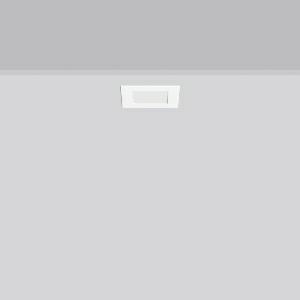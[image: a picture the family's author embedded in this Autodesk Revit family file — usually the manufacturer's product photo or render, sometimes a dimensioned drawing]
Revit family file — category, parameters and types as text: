
# Revit family: toledo_flat_square_e_672241_002_89_4ca7
name_source: partatom
category: Lighting Fixtures
units: mm (PartAtom-declared; Revit-internal decimal feet)

## family parameters
Cut with Voids When Loaded = No
Host = Face
Light Source = No
Part Type = Normal
Room Calculation Point = No
Round Connector Dimension = Use Diameter
Shared = No

## types (1)
- TOLEDO FLAT square E (1 x LED Modul 830, 370 lm, 3000)
    Apparent Load = 6 VA
    CIE Flux Codes = 49 80 96 100 100
    Color Rendering = 80
    Color Temperature = 3000
    Default Elevation = 1800 mm
    Description = Series: TOLEDO FLAT square
Square recessed downlight. For escape route illumination. Housing: die-cast aluminium, powder-coated. Lightguide and diffuser made of non-yellowing plastic (PMMA). Diffuser opal matt plastic. Ceiling installation with spring system. Including separate LED converter with connecting cable 250 mm. Suitable for connection to central battery systems. With AC Control monitoring module for LUXIFAIR central battery units. External driver with simple plug-in locking system. 
Colour: white
Length: 110 mm
Width: 110 mm
Height: 3 mm
Cut-out length: 96 mm
Cut-out width: 96 mm
Recess height: 100 mm
Luminaire: recess height: 37-57 mm
Weight: 1.03 kg
Operating mode: maintained power mode
Lamp: LED
Socket: without socket
Colour temperature: 3000K
Colour rendering index (CRI): 80
System power: 5.7 W
Rated luminous flux: 370 lm
Luminous flux, emergency: 370 lm
System power, emergency: 5.7 W
Control gear: Regulated power supply
Protection class: I
Type of protection: IP 54
    Height = 0 mm  [stored 0 ft]
    Lamp = 1 x LED Modul 830
    Lamp Light Flux = 370 lm
    Lamp count = 1
    Length = 110 mm
    Lifetime = 50000 h
    Luminous efficacy = 65 lm/W
    Manufacturer = RZB
    ModVariant = No
    Model = 672241.002.89
    Mounting Place = Ceiling
    Mounting Type = Recessed
    Number of Poles = 1
    OnlyDefault = Yes
    Power Factor = 1
    Product Name = TOLEDO FLAT square E
    Product group = Recessed downlights
    ProductGroupID = 402
    Protection Class = Protection class I
    Protection Degree = IP 40
    RLX_Detail_Level = 1
    RLX_Emergency_Light_Flux = 370 lm
    RLX_Emergency_Type = 3
    RLX_Emergency_Type_DB = Yes
    RlxData = <blob elided: 9725 chars, md5=e73880e1>
    Socket = socket
    Standby Power = 0 W
    System Light Flux = 370 lm
    System Power = 6 W
    Type Comments = Product without accessories
    Type Image = 901485.002.jpg
    URL = http://relux.com
    VarID = ---
    Voltage = 230 V
    Voltage Range = 220-240 V
    Weight = 0.00 kg
    Width = 110 mm

note: [stored X ft] marks values corroborated as IEEE doubles in the binary element streams (Revit-internal decimal feet)

## geometry (parser evidence)
native form markers: Sweep x11
no freeform markers — native parametric forms only
